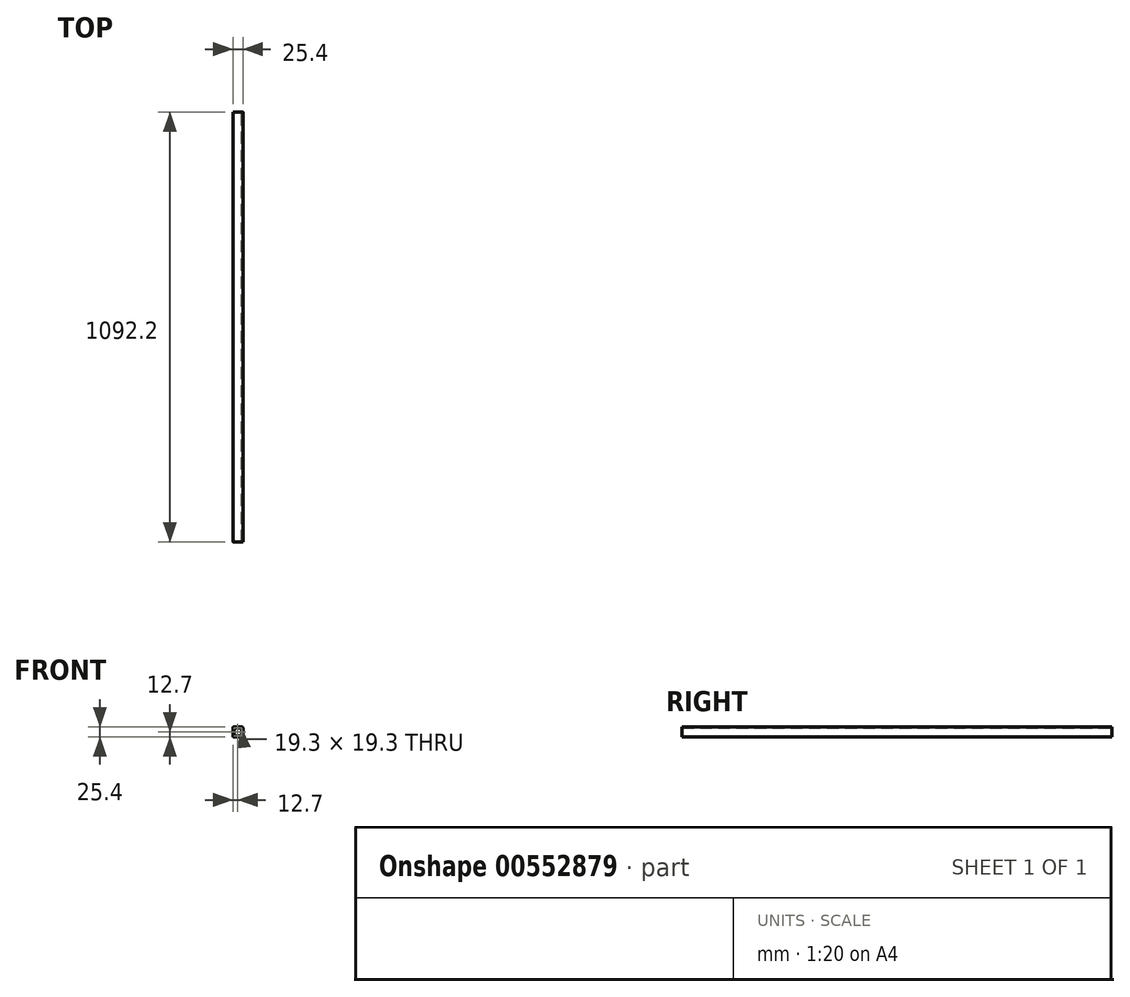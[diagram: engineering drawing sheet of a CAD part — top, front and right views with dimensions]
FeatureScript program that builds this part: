
annotation { "Feature Type Name" : "Feature", "Feature Type Description" : "" }
export const myFeature = defineFeature(function(context is Context, id is Id, definition is map)
    precondition{}
    {
        {
            var Q0;
            Q0=qCreatedBy(makeId("Front.planeOp"),FACE);
            var sketch = newSketch(context, id + "F0", { "sketchPlane" : qUnion([Q0])});
            skLineSegment(sketch, "E0.bottom", {"start": v(10.16, 12.7) * mm, "end": v(-10.16, 12.7) * mm});
            skLineSegment(sketch, "E0.top", {"start": v(10.16, -12.7) * mm, "end": v(-10.16, -12.7) * mm});
            skLineSegment(sketch, "E0.left", {"start": v(12.7, 10.16) * mm, "end": v(12.7, -10.16) * mm});
            skLineSegment(sketch, "E0.right", {"start": v(-12.7, 10.16) * mm, "end": v(-12.7, -10.16) * mm});
            skPoint(sketch, "E0.middle", {"position": v(0, 0) * mm});
            skPoint(sketch, "E1.visualSharp", {"position": v(-12.7, 12.7) * mm});
            skArc(sketch, "E1.filletArc", {"start": v(-10.16, 12.7) * mm, "mid": v(-11.96, 11.96) * mm, "end": v(-12.7, 10.16) * mm});
            skPoint(sketch, "E2.visualSharp", {"position": v(12.7, 12.7) * mm});
            skArc(sketch, "E2.filletArc", {"start": v(12.7, 10.16) * mm, "mid": v(11.96, 11.96) * mm, "end": v(10.16, 12.7) * mm});
            skPoint(sketch, "E3.visualSharp", {"position": v(-12.7, -12.7) * mm});
            skArc(sketch, "E3.filletArc", {"start": v(-12.7, -10.16) * mm, "mid": v(-11.96, -11.96) * mm, "end": v(-10.16, -12.7) * mm});
            skPoint(sketch, "E4.visualSharp", {"position": v(12.7, -12.7) * mm});
            skArc(sketch, "E4.filletArc", {"start": v(10.16, -12.7) * mm, "mid": v(11.96, -11.96) * mm, "end": v(12.7, -10.16) * mm});
            skLineSegment(sketch, "E5.bottom", {"start": v(9.65, 9.65) * mm, "end": v(-9.65, 9.65) * mm});
            skLineSegment(sketch, "E5.top", {"start": v(9.65, -9.65) * mm, "end": v(-9.65, -9.65) * mm});
            skLineSegment(sketch, "E5.left", {"start": v(9.65, 9.65) * mm, "end": v(9.65, -9.65) * mm});
            skLineSegment(sketch, "E5.right", {"start": v(-9.65, 9.65) * mm, "end": v(-9.65, -9.65) * mm});
            skSolve(sketch);
        }
        {
            var Q0;
            Q0 = qSketchRegion(id + "F0", true);
            extrude(context, id + "F1", {"entities" : qUnion([Q0]), "depth" : 1092.2 * mm, "offsetDistance" : 25.4 * mm});
        }
    });
